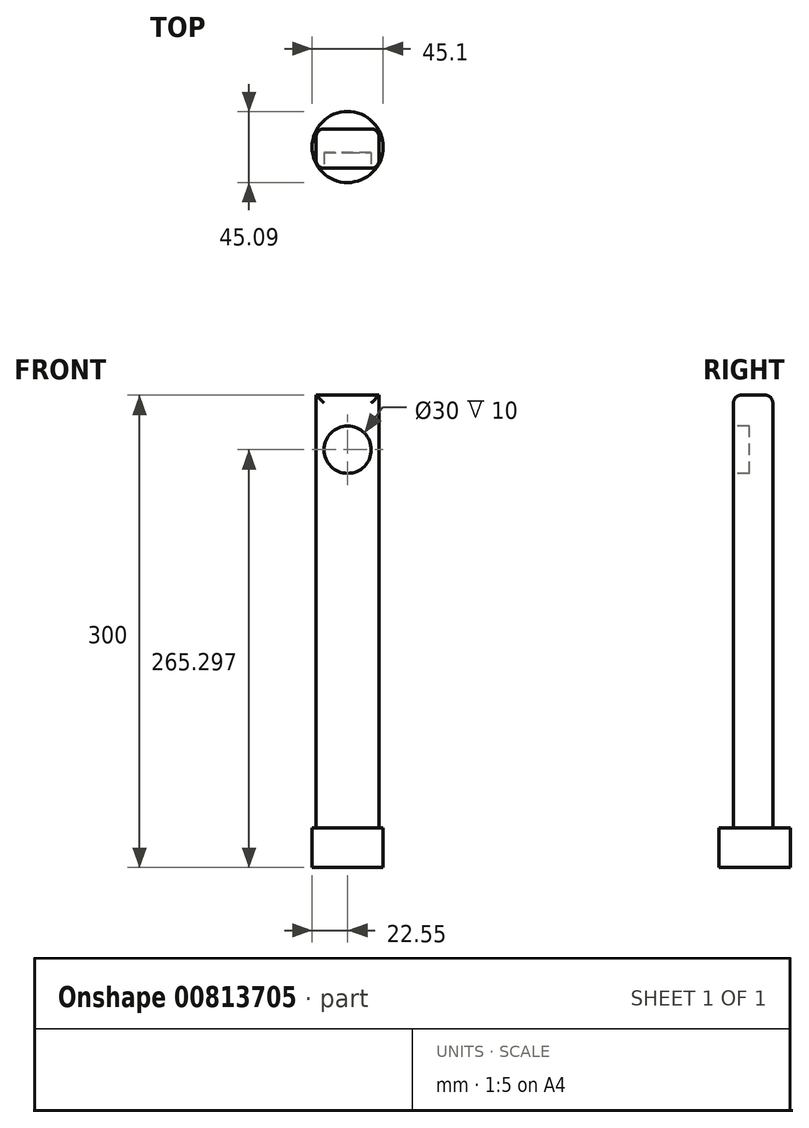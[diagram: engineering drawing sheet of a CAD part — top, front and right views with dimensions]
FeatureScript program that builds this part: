
annotation { "Feature Type Name" : "Feature", "Feature Type Description" : "" }
export const myFeature = defineFeature(function(context is Context, id is Id, definition is map)
    precondition{}
    {
        {
            var Q0;
            Q0=qCreatedBy(makeId("Front.planeOp"),FACE);
            var sketch = newSketch(context, id + "F0", { "sketchPlane" : qUnion([Q0])});
            skLineSegment(sketch, "E0.bottom", {"start": v(-20, 182.5) * mm, "end": v(20, 182.5) * mm});
            skLineSegment(sketch, "E0.top", {"start": v(-20, -117.5) * mm, "end": v(20, -117.5) * mm});
            skLineSegment(sketch, "E0.left", {"start": v(-20, 182.5) * mm, "end": v(-20, -117.5) * mm});
            skLineSegment(sketch, "E0.right", {"start": v(20, 182.5) * mm, "end": v(20, -117.5) * mm});
            skSolve(sketch);
        }
        {
            var Q0;
            Q0=makeQuery(id+"F0.imprint","IMPRINT",FACE,{"disambiguationData":[TD([[makeQuery(id+"F0.imprint","IMPRINT",EDGE,{"derivedFrom":sQuery(id+"F0.wireOp",EDGE,"E0.bottom")}),-1.0]])]});
            extrude(context, id + "F1", {"entities" : qUnion([Q0]), "oppositeDirection" : true, "depth" : 25 * mm, "offsetDistance" : 25 * mm});
        }
        {
            var Q0;
            Q0=qCreatedBy(makeId("Front.planeOp"),FACE);
            var sketch = newSketch(context, id + "F2", { "sketchPlane" : qUnion([Q0])});
            skCircle(sketch, "E1", {"center": v(0, 147.8) * mm, "radius": 15 * mm});
            skSolve(sketch);
        }
        {
            var Q0;
            Q0=makeQuery(id+"F2.imprint","IMPRINT",FACE,{"disambiguationData":[TD([[makeQuery(id+"F2.imprint","IMPRINT",EDGE,{"derivedFrom":sQuery(id+"F2.wireOp",EDGE,"E1")}),1.0]])]});
            extrude(context, id + "F3", {"entities" : qUnion([Q0]), "operationType" : NewBodyOperationType.REMOVE, "oppositeDirection" : true, "depth" : 10 * mm, "offsetDistance" : 25 * mm});
        }
        {
            var Q0;
            Q0=makeQuery(id+"F1.opExtrude","CAP_EDGE",EDGE,{"disambiguationData":[OSD([sQuery(id+"F0.wireOp",EDGE,"E0.right")])],"isStart":false});
            var Q1;
            Q1=makeQuery(id+"F1.opExtrude","CAP_EDGE",EDGE,{"disambiguationData":[OSD([sQuery(id+"F0.wireOp",EDGE,"E0.left")])],"isStart":false});
            var Q2;
            Q2=makeQuery(id+"F1.opExtrude","CAP_EDGE",EDGE,{"disambiguationData":[OSD([sQuery(id+"F0.wireOp",EDGE,"E0.bottom")])],"isStart":false});
            fillet(context, id + "F4", {"entities" : qUnion([Q0, Q1, Q2]), "radius" : 5 * mm, "tangentPropagation" : true, "allowEdgeOverflow" : false});
        }
        {
            var Q0;
            Q0=makeQuery(id+"F1.opExtrude","CAP_EDGE",EDGE,{"disambiguationData":[OSD([sQuery(id+"F0.wireOp",EDGE,"E0.right")])],"isStart":true});
            var Q1;
            Q1=makeQuery(id+"F1.opExtrude","CAP_EDGE",EDGE,{"disambiguationData":[OSD([sQuery(id+"F0.wireOp",EDGE,"E0.left")])],"isStart":true});
            var Q2;
            Q2=makeQuery(id+"F1.opExtrude","CAP_EDGE",EDGE,{"disambiguationData":[OSD([sQuery(id+"F0.wireOp",EDGE,"E0.bottom")])],"isStart":true});
            fillet(context, id + "F5", {"entities" : qUnion([Q0, Q1, Q2]), "radius" : 5 * mm, "tangentPropagation" : true, "allowEdgeOverflow" : false});
        }
        {
            var Q0;
            Q0=makeQuery(id+"F1.opExtrude","SWEPT_FACE",FACE,{"disambiguationData":[OSD([sQuery(id+"F0.wireOp",EDGE,"E0.top")])]});
            var sketch = newSketch(context, id + "F6", { "sketchPlane" : qUnion([Q0])});
            skCircle(sketch, "E2", {"center": v(0, -13.46) * mm, "radius": 22.55 * mm});
            skSolve(sketch);
        }
        {
            var Q0;
            Q0 = qSketchRegion(id + "F6", true);
            extrude(context, id + "F7", {"entities" : qUnion([Q0]), "operationType" : NewBodyOperationType.ADD, "oppositeDirection" : true, "depth" : 25 * mm, "offsetDistance" : 25 * mm});
        }
    });
